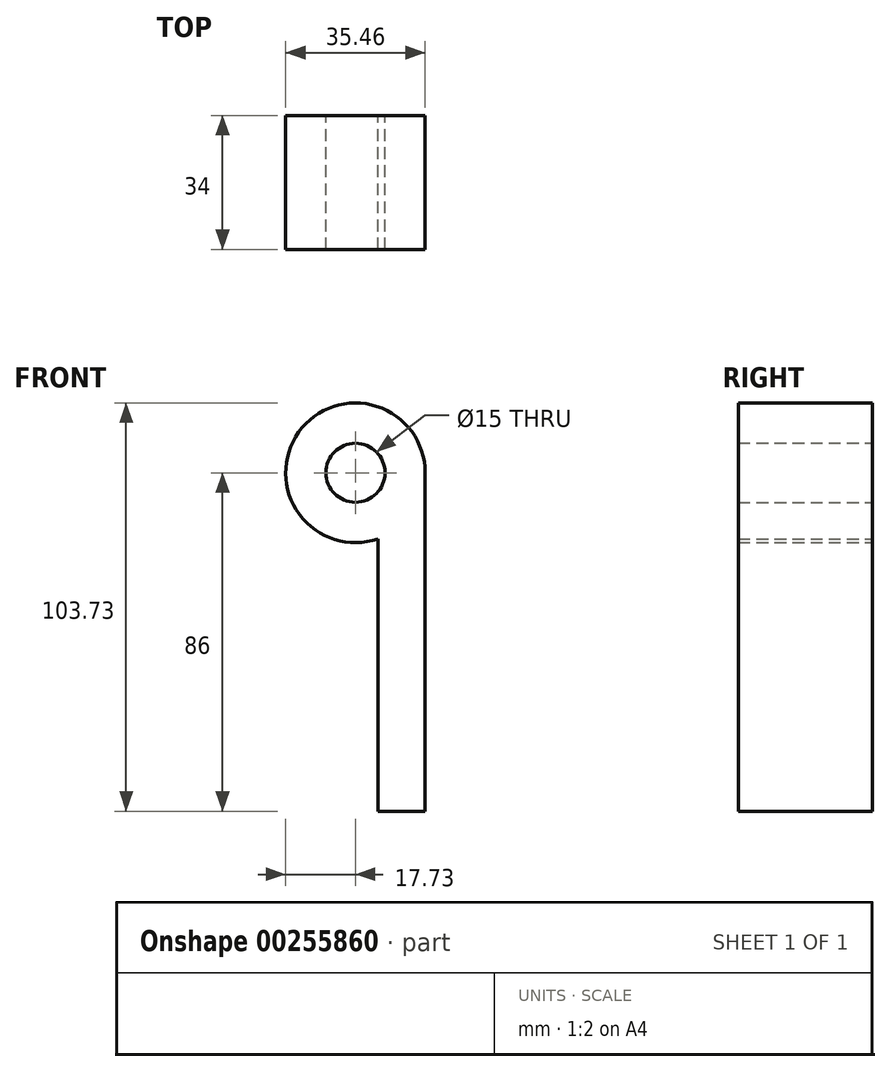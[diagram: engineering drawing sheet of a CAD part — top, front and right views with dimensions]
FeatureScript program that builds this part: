
annotation { "Feature Type Name" : "Feature", "Feature Type Description" : "" }
export const myFeature = defineFeature(function(context is Context, id is Id, definition is map)
    precondition{}
    {
        {
            var Q0;
            Q0=qCreatedBy(makeId("Front.planeOp"),FACE);
            var sketch = newSketch(context, id + "F0", { "sketchPlane" : qUnion([Q0])});
            skArc(sketch, "E0", {"start": v(17.73, 0) * mm, "mid": v(-14.42, 10.31) * mm, "end": v(5.73, -16.78) * mm});
            skCircle(sketch, "E1", {"center": v(0, 0) * mm, "radius": 7.5 * mm});
            skLineSegment(sketch, "E2.bottom", {"start": v(17.73, -86) * mm, "end": v(5.73, -86) * mm});
            skLineSegment(sketch, "E2.left", {"start": v(17.73, -86) * mm, "end": v(17.73, 0) * mm});
            skLineSegment(sketch, "E2.right", {"start": v(5.73, -86) * mm, "end": v(5.73, -16.78) * mm});
            skPoint(sketch, "E2.middle", {"position": v(11.73, -43) * mm});
            skPoint(sketch, "E3.orphan", {"position": v(5.73, 0) * mm});
            skSolve(sketch);
        }
        {
            var Q0;
            Q0 = qSketchRegion(id + "F0", true);
            extrude(context, id + "F1", {"entities" : qUnion([Q0]), "endBound" : BoundingType.SYMMETRIC, "depth" : 34 * mm});
        }
        {
            var Q0;
            Q0=qCreatedBy(makeId("Right.planeOp"),FACE);
            cPlane(context, id + "F2", {"entities" : qUnion([Q0]), "cplaneType" : CPlaneType.OFFSET, "offset" : 79.6 * mm, "oppositeDirection" : true, "width" : 150 * mm, "height" : 150 * mm});
        }
    });
